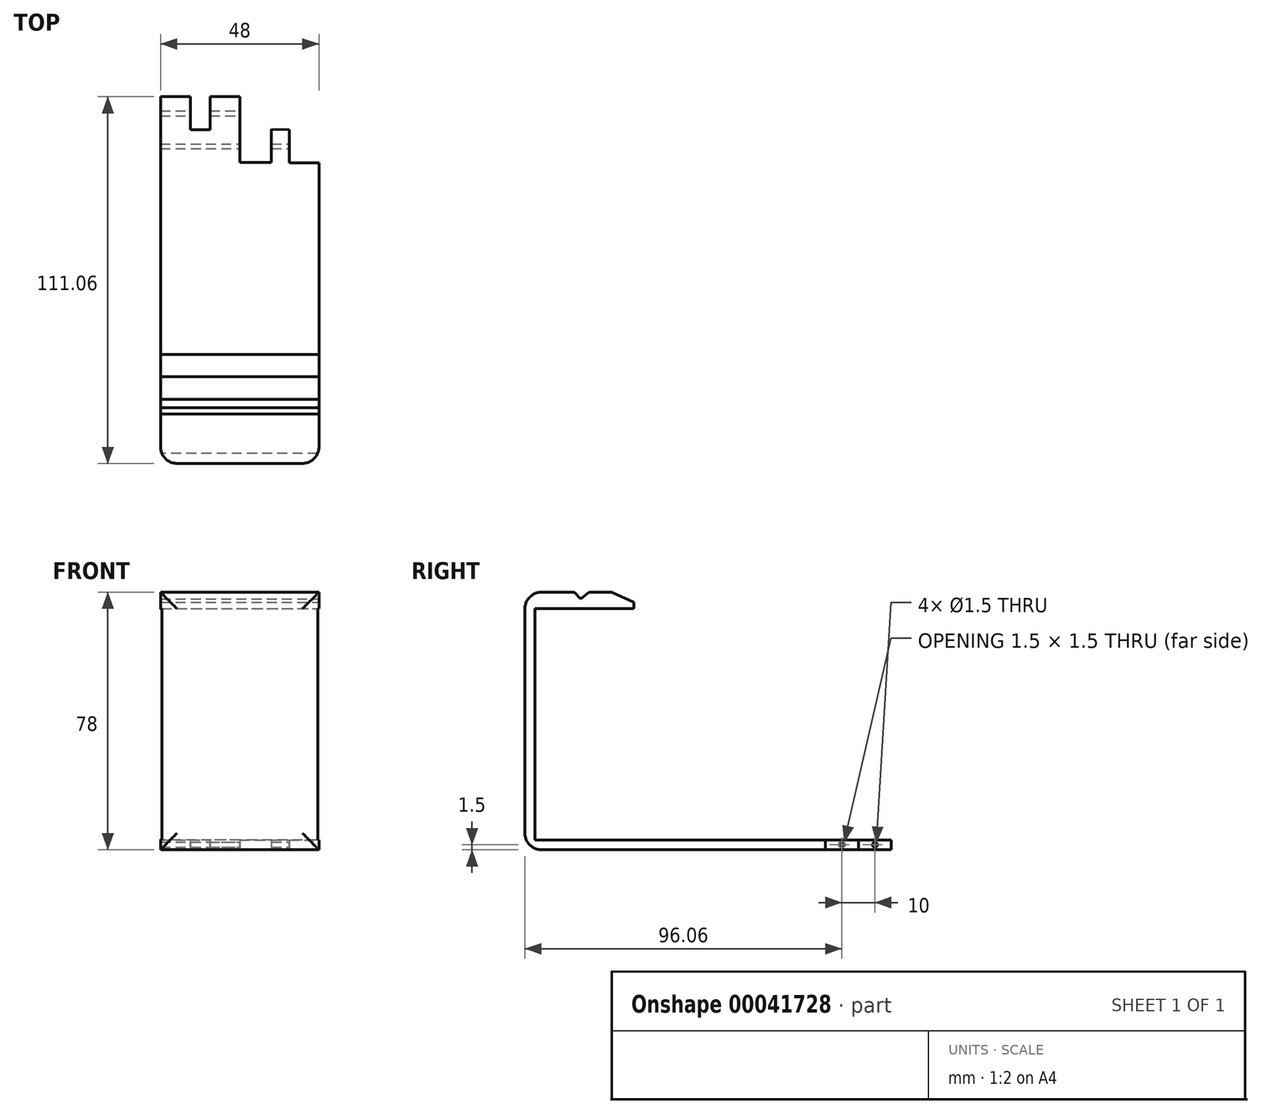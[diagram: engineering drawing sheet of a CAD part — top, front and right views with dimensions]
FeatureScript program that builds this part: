
annotation { "Feature Type Name" : "Feature", "Feature Type Description" : "" }
export const myFeature = defineFeature(function(context is Context, id is Id, definition is map)
    precondition{}
    {
        {
            var Q0;
            Q0=qCreatedBy(makeId("Top.planeOp"),FACE);
            var sketch = newSketch(context, id + "F0", { "sketchPlane" : qUnion([Q0])});
            skLineSegment(sketch, "E0", {"start": v(0, 0) * mm, "end": v(-24, 0) * mm});
            skLineSegment(sketch, "E1", {"start": v(-24, 0) * mm, "end": v(-24, 108) * mm});
            skLineSegment(sketch, "E2", {"start": v(-24, 108) * mm, "end": v(-15, 108) * mm});
            skLineSegment(sketch, "E3", {"start": v(-15, 108) * mm, "end": v(-15, 98) * mm});
            skLineSegment(sketch, "E4", {"start": v(15, 98) * mm, "end": v(15, 88) * mm});
            skLineSegment(sketch, "E5", {"start": v(15, 88) * mm, "end": v(24, 88) * mm});
            skLineSegment(sketch, "E6", {"start": v(24, 88) * mm, "end": v(24, 0) * mm});
            skLineSegment(sketch, "E7", {"start": v(24, 0) * mm, "end": v(0, 0) * mm});
            skLineSegment(sketch, "E8", {"start": v(0, 108) * mm, "end": v(-9, 108) * mm});
            skLineSegment(sketch, "E9", {"start": v(-9, 108) * mm, "end": v(-9, 98) * mm});
            skLineSegment(sketch, "E10", {"start": v(-15, 98) * mm, "end": v(-9, 98) * mm});
            skLineSegment(sketch, "E11", {"start": v(0, 88.08) * mm, "end": v(9.6, 88.08) * mm});
            skLineSegment(sketch, "E12", {"start": v(9.6, 88.08) * mm, "end": v(9.6, 98.08) * mm});
            skLineSegment(sketch, "E13", {"start": v(9.6, 98.08) * mm, "end": v(15, 98) * mm});
            skLineSegment(sketch, "E14", {"start": v(0, 108) * mm, "end": v(0, 88.08) * mm});
            skSolve(sketch);
        }
        {
            var Q0;
            Q0=makeQuery(id+"F0.imprint","IMPRINT",FACE,{"disambiguationData":[TD([[makeQuery(id+"F0.imprint","IMPRINT",EDGE,{"derivedFrom":sQuery(id+"F0.wireOp",EDGE,"E0")}),-1.0]])]});
            extrude(context, id + "F1", {"entities" : qUnion([Q0]), "depth" : 3 * mm});
        }
        {
            var Q0;
            Q0=makeQuery(id+"F1.opExtrude","SWEPT_FACE",FACE,{"disambiguationData":[OSD([sQuery(id+"F0.wireOp",EDGE,"E6")])]});
            var sketch = newSketch(context, id + "F2", { "sketchPlane" : qUnion([Q0])});
            skLineSegment(sketch, "E15", {"start": v(0, 0) * mm, "end": v(0, 73) * mm});
            skLineSegment(sketch, "E16", {"start": v(0, 0) * mm, "end": v(-3.06, 0) * mm});
            skLineSegment(sketch, "E17", {"start": v(-3.06, 0) * mm, "end": v(-3.06, 78) * mm});
            skLineSegment(sketch, "E18", {"start": v(-3.06, 78) * mm, "end": v(11.94, 78) * mm});
            skLineSegment(sketch, "E19", {"start": v(0, 73) * mm, "end": v(30, 73) * mm});
            skLineSegment(sketch, "E20", {"start": v(30, 75) * mm, "end": v(30, 73) * mm});
            skLineSegment(sketch, "E21", {"start": v(11.94, 78) * mm, "end": v(13.87, 76) * mm});
            skLineSegment(sketch, "E22", {"start": v(30, 75) * mm, "end": v(23.26, 78) * mm});
            skLineSegment(sketch, "E23", {"start": v(23.26, 78) * mm, "end": v(16.37, 78) * mm});
            skLineSegment(sketch, "E24", {"start": v(13.87, 76) * mm, "end": v(16.37, 78) * mm});
            skSolve(sketch);
        }
        {
            var Q0;
            Q0=qSketchRegion(id+"F2",true);
            extrude(context, id + "F3", {"entities" : qUnion([Q0]), "operationType" : NewBodyOperationType.ADD, "oppositeDirection" : true, "depth" : 48 * mm});
        }
        {
            var Q0;
            Q0=makeQuery(id+"F3.boolean.opBoolean","MERGE",FACE,{"derivedFrom":[makeQuery(id+"F1.opExtrude","SWEPT_FACE",FACE,{"disambiguationData":[OSD([sQuery(id+"F0.wireOp",EDGE,"E0"),sQuery(id+"F0.wireOp",EDGE,"E7")])]}),makeQuery(id+"F3.opExtrude","SWEPT_FACE",FACE,{"disambiguationData":[OSD([sQuery(id+"F2.wireOp",EDGE,"E15")])]})]});
            var Q1;
            Q1=makeQuery(id+"F3.opExtrude","SWEPT_FACE",FACE,{"disambiguationData":[OSD([sQuery(id+"F2.wireOp",EDGE,"E17")])]});
            fillet(context, id + "F4", {"entities" : qUnion([Q0, Q1]), "radius" : 5 * mm, "tangentPropagation" : true, "allowEdgeOverflow" : false});
        }
        {
            var Q0;
            Q0=makeQuery(id+"F1.opExtrude","SWEPT_FACE",FACE,{"disambiguationData":[OSD([sQuery(id+"F0.wireOp",EDGE,"E4")])]});
            var sketch = newSketch(context, id + "F5", { "sketchPlane" : qUnion([Q0])});
            skLineSegment(sketch, "E25", {"start": v(88, 1.5) * mm, "end": v(98, 1.5) * mm, "construction": true});
            skCircle(sketch, "E26", {"center": v(93, 1.5) * mm, "radius": 0.75 * mm});
            skSolve(sketch);
        }
        {
            var Q0;
            Q0=qSketchRegion(id+"F5",true);
            extrude(context, id + "F6", {"entities" : qUnion([Q0]), "operationType" : NewBodyOperationType.REMOVE, "endBound" : BoundingType.THROUGH_ALL, "oppositeDirection" : true, "depth" : 25 * mm});
        }
        {
            var Q0;
            Q0=makeQuery(id+"F1.opExtrude","SWEPT_FACE",FACE,{"disambiguationData":[OSD([sQuery(id+"F0.wireOp",EDGE,"E3")])]});
            var sketch = newSketch(context, id + "F7", { "sketchPlane" : qUnion([Q0])});
            skLineSegment(sketch, "E27", {"start": v(108, 1.5) * mm, "end": v(98, 1.5) * mm, "construction": true});
            skCircle(sketch, "E28", {"center": v(103, 1.5) * mm, "radius": 0.75 * mm});
            skSolve(sketch);
        }
        {
            var Q0;
            Q0=qSketchRegion(id+"F7",true);
            extrude(context, id + "F8", {"entities" : qUnion([Q0]), "operationType" : NewBodyOperationType.REMOVE, "endBound" : BoundingType.THROUGH_ALL, "oppositeDirection" : true, "depth" : 25 * mm, "hasSecondDirection" : true, "secondDirectionBound" : SecondDirectionBoundingType.THROUGH_ALL, "secondDirectionOppositeDirection" : false, "secondDirectionDepth" : 25 * mm});
        }
    });
